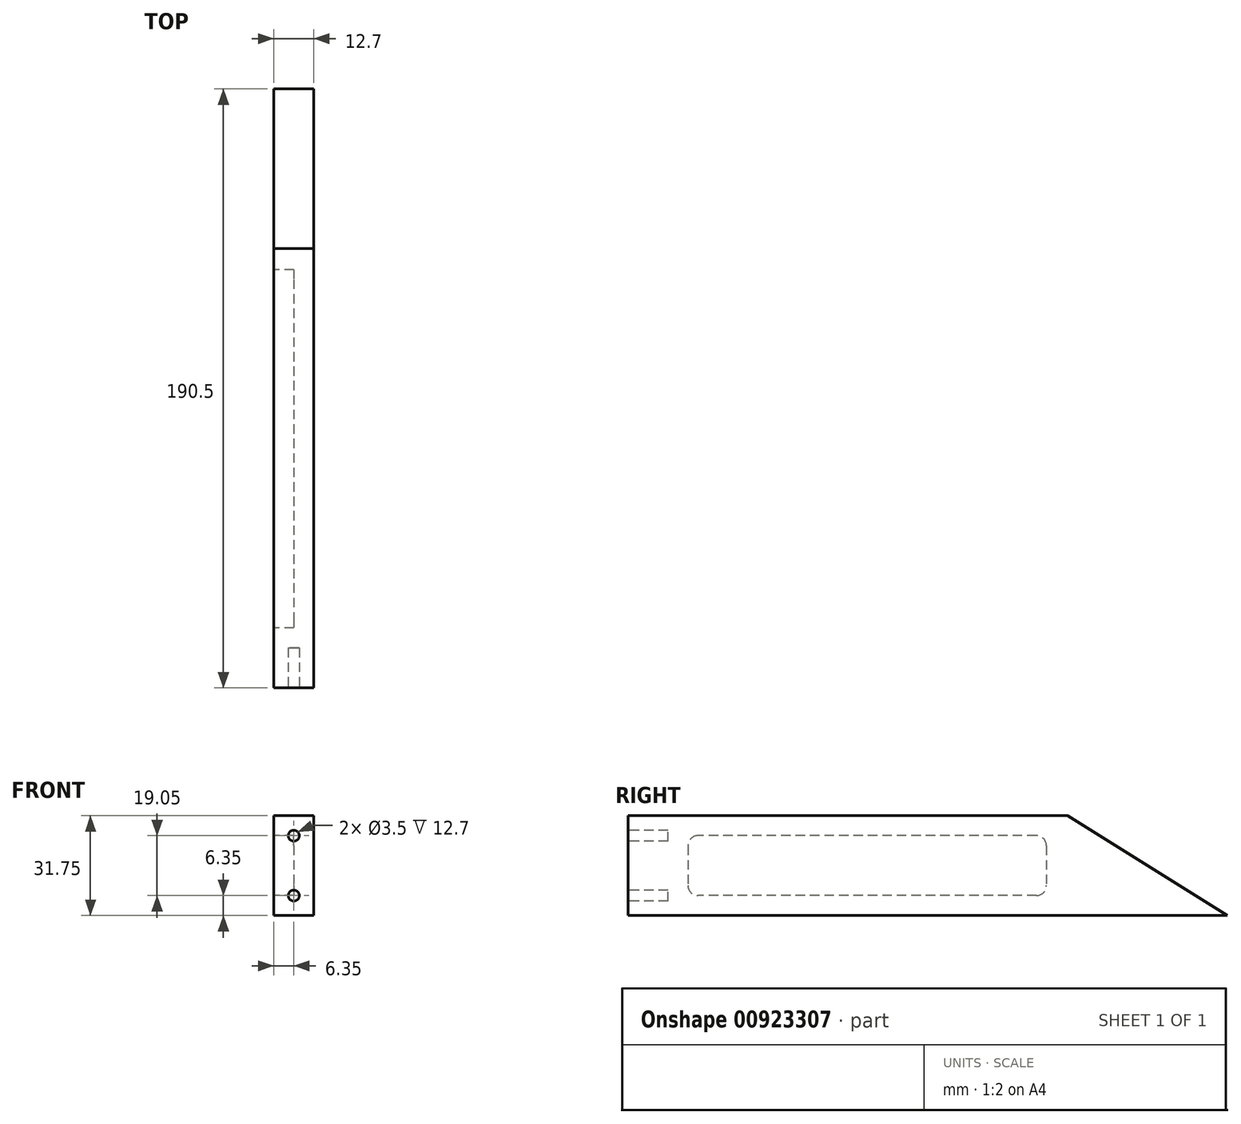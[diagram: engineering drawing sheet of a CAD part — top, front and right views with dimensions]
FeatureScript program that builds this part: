
annotation { "Feature Type Name" : "Feature", "Feature Type Description" : "" }
export const myFeature = defineFeature(function(context is Context, id is Id, definition is map)
    precondition{}
    {
        {
            var Q0;
            Q0=qCreatedBy(makeId("Right.planeOp"),FACE);
            var sketch = newSketch(context, id + "F0", { "sketchPlane" : qUnion([Q0])});
            skLineSegment(sketch, "E0.bottom", {"start": v(0, 0) * mm, "end": v(190.5, 0) * mm});
            skLineSegment(sketch, "E0.top", {"start": v(0, 31.75) * mm, "end": v(190.5, 31.75) * mm});
            skLineSegment(sketch, "E0.left", {"start": v(0, 0) * mm, "end": v(0, 31.75) * mm});
            skLineSegment(sketch, "E0.right", {"start": v(190.5, 0) * mm, "end": v(190.5, 31.75) * mm});
            skSolve(sketch);
        }
        {
            var Q0;
            Q0 = qSketchRegion(id + "F0", true);
            extrude(context, id + "F1", {"entities" : qUnion([Q0]), "depth" : 12.7 * mm, "offsetDistance" : 25.4 * mm});
        }
        {
            var Q0;
            Q0=makeQuery(id+"F1.opExtrude","CAP_FACE",FACE,{"disambiguationData":[OSD([sQuery(id+"F0.wireOp",EDGE,"E0.bottom"),sQuery(id+"F0.wireOp",EDGE,"E0.top"),sQuery(id+"F0.wireOp",EDGE,"E0.left"),sQuery(id+"F0.wireOp",EDGE,"E0.right")])],"isStart":false});
            var sketch = newSketch(context, id + "F2", { "sketchPlane" : qUnion([Q0])});
            skLineSegment(sketch, "E1", {"start": v(190.5, 0) * mm, "end": v(190.5, 31.75) * mm});
            skLineSegment(sketch, "E2", {"start": v(190.5, 31.75) * mm, "end": v(139.7, 31.75) * mm});
            skLineSegment(sketch, "E3", {"start": v(139.7, 31.75) * mm, "end": v(190.5, 0) * mm});
            skLineSegment(sketch, "E4", {"start": v(139.7, 31.75) * mm, "end": v(190.5, 31.75) * mm});
            skSolve(sketch);
        }
        {
            var Q0;
            Q0 = qSketchRegion(id + "F2", true);
            extrude(context, id + "F3", {"entities" : qUnion([Q0]), "operationType" : NewBodyOperationType.REMOVE, "oppositeDirection" : true, "depth" : 25.4 * mm, "offsetDistance" : 25.4 * mm});
        }
        {
            var Q0;
            Q0=makeQuery(id+"F1.opExtrude","SWEPT_FACE",FACE,{"disambiguationData":[OSD([sQuery(id+"F0.wireOp",EDGE,"E0.left")])]});
            var sketch = newSketch(context, id + "F4", { "sketchPlane" : qUnion([Q0])});
            skLineSegment(sketch, "E5", {"start": v(6.35, 31.75) * mm, "end": v(6.35, 0) * mm, "construction": true});
            skLineSegment(sketch, "E6", {"start": v(0, 25.4) * mm, "end": v(12.7, 25.4) * mm, "construction": true});
            skLineSegment(sketch, "E7", {"start": v(0, 6.35) * mm, "end": v(12.7, 6.35) * mm, "construction": true});
            skCircle(sketch, "E8", {"center": v(6.35, 25.4) * mm, "radius": 1.75 * mm});
            skCircle(sketch, "E9", {"center": v(6.35, 6.35) * mm, "radius": 1.75 * mm});
            skSolve(sketch);
        }
        {
            var Q0;
            Q0=makeQuery(id+"F4.imprint","IMPRINT",FACE,{"disambiguationData":[TD([[makeQuery(id+"F4.imprint","IMPRINT",EDGE,{"derivedFrom":sQuery(id+"F4.wireOp",EDGE,"E9")}),1.0]])]});
            var Q1;
            Q1=makeQuery(id+"F4.imprint","IMPRINT",FACE,{"disambiguationData":[TD([[makeQuery(id+"F4.imprint","IMPRINT",EDGE,{"derivedFrom":sQuery(id+"F4.wireOp",EDGE,"E8")}),1.0]])]});
            extrude(context, id + "F5", {"entities" : qUnion([Q0, Q1]), "operationType" : NewBodyOperationType.REMOVE, "oppositeDirection" : true, "depth" : 12.7 * mm, "offsetDistance" : 25.4 * mm});
        }
        {
            var Q0;
            Q0=makeQuery(id+"F1.opExtrude","CAP_FACE",FACE,{"disambiguationData":[OSD([sQuery(id+"F0.wireOp",EDGE,"E0.bottom"),sQuery(id+"F0.wireOp",EDGE,"E0.top"),sQuery(id+"F0.wireOp",EDGE,"E0.left"),sQuery(id+"F0.wireOp",EDGE,"E0.right")])],"isStart":true});
            var sketch = newSketch(context, id + "F6", { "sketchPlane" : qUnion([Q0])});
            skLineSegment(sketch, "E10.bottom", {"start": v(-133.02, 25.4) * mm, "end": v(-19.05, 25.4) * mm});
            skLineSegment(sketch, "E10.top", {"start": v(-133.02, 6.35) * mm, "end": v(-19.05, 6.35) * mm});
            skLineSegment(sketch, "E10.left", {"start": v(-133.02, 25.4) * mm, "end": v(-133.02, 6.35) * mm});
            skLineSegment(sketch, "E10.right", {"start": v(-19.05, 25.4) * mm, "end": v(-19.05, 6.35) * mm});
            skSolve(sketch);
        }
        {
            var Q0;
            Q0=makeQuery(id+"F6.imprint","IMPRINT",FACE,{"disambiguationData":[TD([[makeQuery(id+"F6.imprint","IMPRINT",EDGE,{"derivedFrom":sQuery(id+"F6.wireOp",EDGE,"E10.bottom")}),-1.0]])]});
            extrude(context, id + "F7", {"entities" : qUnion([Q0]), "operationType" : NewBodyOperationType.REMOVE, "oppositeDirection" : true, "depth" : 6.35 * mm, "offsetDistance" : 25.4 * mm});
        }
        {
            var Q0;
            Q0=makeQuery(id+"F7.boolean.opBoolean","COPY",EDGE,{"derivedFrom":makeQuery(id+"F7.opExtrude","SWEPT_EDGE",EDGE,{"disambiguationData":[OSD([sQuery(id+"F6.wireOp",EDGE,"E10.bottom"),sQuery(id+"F6.wireOp",EDGE,"E10.left")])]})});
            var Q1;
            Q1=makeQuery(id+"F7.boolean.opBoolean","COPY",EDGE,{"derivedFrom":makeQuery(id+"F7.opExtrude","SWEPT_EDGE",EDGE,{"disambiguationData":[OSD([sQuery(id+"F6.wireOp",EDGE,"E10.bottom"),sQuery(id+"F6.wireOp",EDGE,"E10.right")])]})});
            var Q2;
            Q2=makeQuery(id+"F7.boolean.opBoolean","COPY",EDGE,{"derivedFrom":makeQuery(id+"F7.opExtrude","SWEPT_EDGE",EDGE,{"disambiguationData":[OSD([sQuery(id+"F6.wireOp",EDGE,"E10.top"),sQuery(id+"F6.wireOp",EDGE,"E10.right")])]})});
            var Q3;
            Q3=makeQuery(id+"F7.boolean.opBoolean","COPY",EDGE,{"derivedFrom":makeQuery(id+"F7.opExtrude","SWEPT_EDGE",EDGE,{"disambiguationData":[OSD([sQuery(id+"F6.wireOp",EDGE,"E10.top"),sQuery(id+"F6.wireOp",EDGE,"E10.left")])]})});
            fillet(context, id + "F8", {"entities" : qUnion([Q0, Q1, Q2, Q3]), "radius" : 3.17 * mm, "tangentPropagation" : true, "allowEdgeOverflow" : false});
        }
    });
